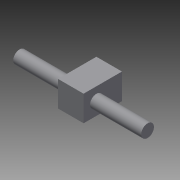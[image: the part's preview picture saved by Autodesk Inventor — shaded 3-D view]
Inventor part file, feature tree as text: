
AUTODESK INVENTOR PART (.ipt)
format: ipt  version: 2014 (Build 180170000, 170)  size: 82,432 bytes
history: native  units: in
note: dims shown in document units (in); Inventor stores cm internally (conversion verified against a paired STEP export)
features: extrude x2, sketch x2
ambient origin geometry x8: Origin, YZ Plane, XZ Plane, XY Plane, X Axis, Y Axis, Z Axis, Center Point
bodies: Solid1 (feature_tree)
feature tree (4):
  extrude  "Extrusion1"  Depth=1.0in
  extrude  "Extrusion2"  Depth=3.0in
  sketch  "Sketch1"  dims[d0=1.5in d1=1.0in]
  sketch  "Sketch2"  dims[d5=1.0in d6=0.0in d7=0.5in d8=0.5in d9=1.0in d10=2.0in d11=3.0in d12=0.0in d13=0.0in]
